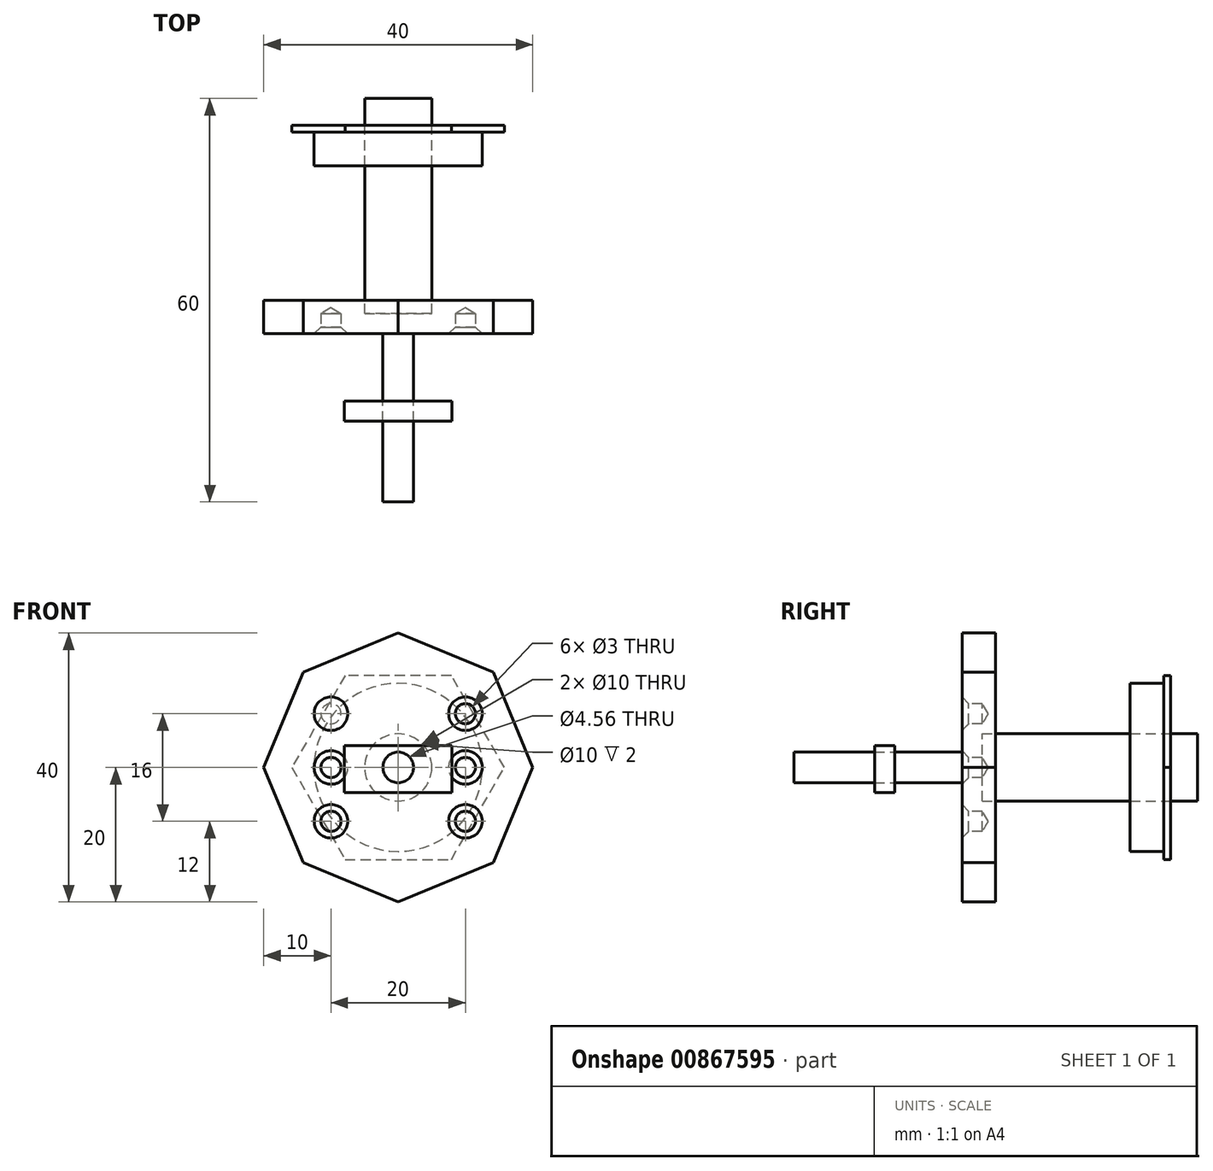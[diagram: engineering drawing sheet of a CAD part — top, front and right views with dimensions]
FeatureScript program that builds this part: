
annotation { "Feature Type Name" : "Feature", "Feature Type Description" : "" }
export const myFeature = defineFeature(function(context is Context, id is Id, definition is map)
    precondition{}
    {
        {
            var Q0;
            Q0=qCreatedBy(makeId("Front.planeOp"),FACE);
            var sketch = newSketch(context, id + "F0", { "sketchPlane" : qUnion([Q0])});
            skCircle(sketch, "E0", {"center": v(0, 0) * mm, "radius": 12.5 * mm});
            skSolve(sketch);
        }
        {
            var Q0;
            Q0 = qSketchRegion(id + "F0", true);
            extrude(context, id + "F1", {"entities" : qUnion([Q0]), "depth" : 5 * mm, "offsetDistance" : 25 * mm});
        }
        {
            var Q0;
            Q0=qCreatedBy(makeId("Front.planeOp"),FACE);
            cPlane(context, id + "F2", {"entities" : qUnion([Q0]), "cplaneType" : CPlaneType.OFFSET, "offset" : 5 * mm, "oppositeDirection" : true, "width" : 150 * mm, "height" : 150 * mm});
        }
        {
            var Q0;
            Q0=qCreatedBy(id+"F2.planeOp",FACE);
            var sketch = newSketch(context, id + "F3", { "sketchPlane" : qUnion([Q0])});
            skCircle(sketch, "E1", {"center": v(0, 0) * mm, "radius": 5 * mm});
            skSolve(sketch);
        }
        {
            var Q0;
            Q0 = qSketchRegion(id + "F3", true);
            extrude(context, id + "F4", {"entities" : qUnion([Q0]), "depth" : 32 * mm, "offsetDistance" : 25 * mm});
        }
        {
            var Q0;
            Q0=qCreatedBy(makeId("Front.planeOp"),FACE);
            cPlane(context, id + "F5", {"entities" : qUnion([Q0]), "cplaneType" : CPlaneType.OFFSET, "offset" : 25 * mm, "width" : 150 * mm, "height" : 150 * mm});
        }
        {
            var Q0;
            Q0=qCreatedBy(id+"F5.planeOp",FACE);
            var sketch = newSketch(context, id + "F6", { "sketchPlane" : qUnion([Q0])});
            skCircle(sketch, "E2.cCircle", {"center": v(0, 0) * mm, "radius": 18.48 * mm, "construction": true});
            skLineSegment(sketch, "E2.0", {"start": v(14.14, 14.14) * mm, "end": v(20, 0) * mm});
            skLineSegment(sketch, "E2.1", {"start": v(20, 0) * mm, "end": v(14.14, -14.14) * mm});
            skLineSegment(sketch, "E2.2", {"start": v(14.14, -14.14) * mm, "end": v(0, -20) * mm});
            skLineSegment(sketch, "E2.3", {"start": v(0, -20) * mm, "end": v(-14.14, -14.14) * mm});
            skLineSegment(sketch, "E2.4", {"start": v(-14.14, -14.14) * mm, "end": v(-20, 0) * mm});
            skLineSegment(sketch, "E2.5", {"start": v(-20, 0) * mm, "end": v(-14.14, 14.14) * mm});
            skLineSegment(sketch, "E2.6", {"start": v(-14.14, 14.14) * mm, "end": v(0, 20) * mm});
            skLineSegment(sketch, "E2.7", {"start": v(0, 20) * mm, "end": v(14.14, 14.14) * mm});
            skPoint(sketch, "E2.0.midPoint", {"position": v(17.07, 7.07) * mm});
            skSolve(sketch);
        }
        {
            var Q0;
            Q0 = qSketchRegion(id + "F6", true);
            extrude(context, id + "F7", {"entities" : qUnion([Q0]), "depth" : 5 * mm, "offsetDistance" : 25 * mm});
        }
        {
            var Q0;
            Q0=makeQuery(id+"F7.opExtrude","CAP_FACE",FACE,{"disambiguationData":[OSD([sQuery(id+"F6.wireOp",EDGE,"E2.0"),sQuery(id+"F6.wireOp",EDGE,"E2.1"),sQuery(id+"F6.wireOp",EDGE,"E2.2"),sQuery(id+"F6.wireOp",EDGE,"E2.3"),sQuery(id+"F6.wireOp",EDGE,"E2.4"),sQuery(id+"F6.wireOp",EDGE,"E2.5"),sQuery(id+"F6.wireOp",EDGE,"E2.6"),sQuery(id+"F6.wireOp",EDGE,"E2.7")])],"isStart":false});
            var sketch = newSketch(context, id + "F8", { "sketchPlane" : qUnion([Q0])});
            skPoint(sketch, "E3", {"position": v(-10, 0) * mm});
            skPoint(sketch, "E4", {"position": v(-10, 8) * mm});
            skPoint(sketch, "E5", {"position": v(-10, -8) * mm});
            skPoint(sketch, "E6.MirrorP", {"position": v(10, 8) * mm});
            skPoint(sketch, "E7.MirrorP", {"position": v(10, 0) * mm});
            skPoint(sketch, "E8.MirrorP", {"position": v(10, -8) * mm});
            skSolve(sketch);
        }
        {
            var Q0;
            Q0=sQuery(id+"F8.wireOp",VERTEX,"E4");
            var Q1;
            Q1=sQuery(id+"F8.wireOp",VERTEX,"E3");
            var Q2;
            Q2=sQuery(id+"F8.wireOp",VERTEX,"E5");
            var Q3;
            Q3=sQuery(id+"F8.wireOp",VERTEX,"E6.MirrorP");
            var Q4;
            Q4=sQuery(id+"F8.wireOp",VERTEX,"E7.MirrorP");
            var Q5;
            Q5=sQuery(id+"F8.wireOp",VERTEX,"E8.MirrorP");
            var Q6;
            Q6=makeQuery(id+"F7.opExtrude","SWEPT_BODY",BODY,{"disambiguationData":[OSD([sQuery(id+"F6.wireOp",EDGE,"E2.0"),sQuery(id+"F6.wireOp",EDGE,"E2.1"),sQuery(id+"F6.wireOp",EDGE,"E2.2"),sQuery(id+"F6.wireOp",EDGE,"E2.3"),sQuery(id+"F6.wireOp",EDGE,"E2.4"),sQuery(id+"F6.wireOp",EDGE,"E2.5"),sQuery(id+"F6.wireOp",EDGE,"E2.6"),sQuery(id+"F6.wireOp",EDGE,"E2.7")])]});
            hole(context, id + "F9", {"style" : HoleStyle.C_SINK, "endStyle" : HoleEndStyle.BLIND, "holeDiameter" : 3 * mm, "cSinkDiameter" : 5 * mm, "cSinkAngle" : 90 * degree, "majorDiameter" : 5 * mm, "holeDepth" : 3 * mm, "isTappedThrough" : true, "tappedDepth" : 12 * mm, "tapClearance" : 3, "startFromSketch" : true, "locations" : qUnion([Q0, Q1, Q2, Q3, Q4, Q5]), "scope" : qUnion([Q6])});
        }
        {
            var Q0;
            Q0=makeQuery(id+"F7.opExtrude","CAP_FACE",FACE,{"disambiguationData":[OSD([sQuery(id+"F6.wireOp",EDGE,"E2.0"),sQuery(id+"F6.wireOp",EDGE,"E2.1"),sQuery(id+"F6.wireOp",EDGE,"E2.2"),sQuery(id+"F6.wireOp",EDGE,"E2.3"),sQuery(id+"F6.wireOp",EDGE,"E2.4"),sQuery(id+"F6.wireOp",EDGE,"E2.5"),sQuery(id+"F6.wireOp",EDGE,"E2.6"),sQuery(id+"F6.wireOp",EDGE,"E2.7")])],"isStart":false});
            var sketch = newSketch(context, id + "F10", { "sketchPlane" : qUnion([Q0])});
            skCircle(sketch, "E9.0", {"center": v(-10, 8) * mm, "radius": 2.5 * mm});
            skSolve(sketch);
        }
        {
            var Q0;
            Q0 = qSketchRegion(id + "F10", true);
            var Q1;
            Q1=makeQuery(id+"F7.opExtrude","CAP_FACE",FACE,{"disambiguationData":[OSD([sQuery(id+"F6.wireOp",EDGE,"E2.0"),sQuery(id+"F6.wireOp",EDGE,"E2.1"),sQuery(id+"F6.wireOp",EDGE,"E2.2"),sQuery(id+"F6.wireOp",EDGE,"E2.3"),sQuery(id+"F6.wireOp",EDGE,"E2.4"),sQuery(id+"F6.wireOp",EDGE,"E2.5"),sQuery(id+"F6.wireOp",EDGE,"E2.6"),sQuery(id+"F6.wireOp",EDGE,"E2.7")])],"isStart":true});
            extrude(context, id + "F11", {"entities" : qUnion([Q0]), "endBound" : BoundingType.UP_TO_SURFACE, "oppositeDirection" : true, "depth" : 3 * mm, "endBoundEntityFace" : qUnion([Q1]), "offsetDistance" : 25 * mm});
        }
        {
            var Q0;
            Q0=makeQuery(id+"F7.opExtrude","SWEPT_BODY",BODY,{"disambiguationData":[OSD([sQuery(id+"F6.wireOp",EDGE,"E2.0"),sQuery(id+"F6.wireOp",EDGE,"E2.1"),sQuery(id+"F6.wireOp",EDGE,"E2.2"),sQuery(id+"F6.wireOp",EDGE,"E2.3"),sQuery(id+"F6.wireOp",EDGE,"E2.4"),sQuery(id+"F6.wireOp",EDGE,"E2.5"),sQuery(id+"F6.wireOp",EDGE,"E2.6"),sQuery(id+"F6.wireOp",EDGE,"E2.7")])]});
            var Q1;
            Q1=makeQuery(id+"F11.opExtrude","SWEPT_BODY",BODY,{"disambiguationData":[OSD([sQuery(id+"F10.wireOp",EDGE,"E9.0")])]});
            booleanBodies(context, id + "F12", {"operationType" : BooleanOperationType.SUBTRACTION, "tools" : qUnion([Q0]), "targets" : qUnion([Q1]), "keepTools" : true});
        }
        {
            var Q0;
            Q0=makeQuery(id+"F4.opExtrude","SWEPT_BODY",BODY,{"disambiguationData":[OSD([sQuery(id+"F3.wireOp",EDGE,"E1")])]});
            var Q1;
            Q1=makeQuery(id+"F7.opExtrude","SWEPT_BODY",BODY,{"disambiguationData":[OSD([sQuery(id+"F6.wireOp",EDGE,"E2.0"),sQuery(id+"F6.wireOp",EDGE,"E2.1"),sQuery(id+"F6.wireOp",EDGE,"E2.2"),sQuery(id+"F6.wireOp",EDGE,"E2.3"),sQuery(id+"F6.wireOp",EDGE,"E2.4"),sQuery(id+"F6.wireOp",EDGE,"E2.5"),sQuery(id+"F6.wireOp",EDGE,"E2.6"),sQuery(id+"F6.wireOp",EDGE,"E2.7")])]});
            booleanBodies(context, id + "F13", {"operationType" : BooleanOperationType.SUBTRACTION, "tools" : qUnion([Q0]), "targets" : qUnion([Q1]), "keepTools" : true});
        }
        {
            var Q0;
            Q0=makeQuery(id+"F4.opExtrude","SWEPT_BODY",BODY,{"disambiguationData":[OSD([sQuery(id+"F3.wireOp",EDGE,"E1")])]});
            var Q1;
            Q1=makeQuery(id+"F1.opExtrude","SWEPT_BODY",BODY,{"disambiguationData":[OSD([sQuery(id+"F0.wireOp",EDGE,"E0")])]});
            booleanBodies(context, id + "F14", {"operationType" : BooleanOperationType.SUBTRACTION, "tools" : qUnion([Q0]), "targets" : qUnion([Q1]), "keepTools" : true});
        }
        {
            var Q0;
            Q0=makeQuery(id+"F1.opExtrude","CAP_FACE",FACE,{"disambiguationData":[OSD([sQuery(id+"F0.wireOp",EDGE,"E0")])],"isStart":true});
            cPlane(context, id + "F15", {"entities" : qUnion([Q0]), "cplaneType" : CPlaneType.OFFSET, "offset" : 0 * mm, "width" : 150 * mm, "height" : 150 * mm});
        }
        {
            var Q0;
            Q0=qCreatedBy(id+"F15.planeOp",FACE);
            var sketch = newSketch(context, id + "F16", { "sketchPlane" : qUnion([Q0])});
            skCircle(sketch, "E10.cCircle", {"center": v(0, 0) * mm, "radius": 13.68 * mm, "construction": true});
            skLineSegment(sketch, "E10.0", {"start": v(15.8, 0) * mm, "end": v(7.9, -13.68) * mm});
            skLineSegment(sketch, "E10.1", {"start": v(7.9, -13.68) * mm, "end": v(-7.9, -13.68) * mm});
            skLineSegment(sketch, "E10.2", {"start": v(-7.9, -13.68) * mm, "end": v(-15.8, 0) * mm});
            skLineSegment(sketch, "E10.3", {"start": v(-15.8, 0) * mm, "end": v(-7.9, 13.68) * mm});
            skLineSegment(sketch, "E10.4", {"start": v(-7.9, 13.68) * mm, "end": v(7.9, 13.68) * mm});
            skLineSegment(sketch, "E10.5", {"start": v(7.9, 13.68) * mm, "end": v(15.8, 0) * mm});
            skPoint(sketch, "E10.0.midPoint", {"position": v(11.85, -6.84) * mm});
            skSolve(sketch);
        }
        {
            var Q0;
            Q0 = qSketchRegion(id + "F16", true);
            extrude(context, id + "F17", {"entities" : qUnion([Q0]), "depth" : 1 * mm, "offsetDistance" : 25 * mm});
        }
        {
            var Q0;
            Q0=makeQuery(id+"F4.opExtrude","SWEPT_BODY",BODY,{"disambiguationData":[OSD([sQuery(id+"F3.wireOp",EDGE,"E1")])]});
            var Q1;
            Q1=makeQuery(id+"F17.opExtrude","SWEPT_BODY",BODY,{"disambiguationData":[OSD([sQuery(id+"F16.wireOp",EDGE,"E10.0"),sQuery(id+"F16.wireOp",EDGE,"E10.1"),sQuery(id+"F16.wireOp",EDGE,"E10.2"),sQuery(id+"F16.wireOp",EDGE,"E10.3"),sQuery(id+"F16.wireOp",EDGE,"E10.4"),sQuery(id+"F16.wireOp",EDGE,"E10.5")])]});
            booleanBodies(context, id + "F18", {"operationType" : BooleanOperationType.SUBTRACTION, "tools" : qUnion([Q0]), "targets" : qUnion([Q1]), "keepTools" : true});
        }
        {
            var Q0;
            Q0=makeQuery(id+"F7.opExtrude","CAP_FACE",FACE,{"disambiguationData":[OSD([sQuery(id+"F6.wireOp",EDGE,"E2.0"),sQuery(id+"F6.wireOp",EDGE,"E2.1"),sQuery(id+"F6.wireOp",EDGE,"E2.2"),sQuery(id+"F6.wireOp",EDGE,"E2.3"),sQuery(id+"F6.wireOp",EDGE,"E2.4"),sQuery(id+"F6.wireOp",EDGE,"E2.5"),sQuery(id+"F6.wireOp",EDGE,"E2.6"),sQuery(id+"F6.wireOp",EDGE,"E2.7")])],"isStart":false});
            var sketch = newSketch(context, id + "F19", { "sketchPlane" : qUnion([Q0])});
            skCircle(sketch, "E11", {"center": v(0, 0) * mm, "radius": 2.28 * mm});
            skSolve(sketch);
        }
        {
            var Q0;
            Q0 = qSketchRegion(id + "F19", true);
            extrude(context, id + "F20", {"entities" : qUnion([Q0]), "operationType" : NewBodyOperationType.ADD, "depth" : 25 * mm, "offsetDistance" : 25 * mm});
        }
        {
            var Q0;
            Q0=qCreatedBy(id+"F5.planeOp",FACE);
            cPlane(context, id + "F21", {"entities" : qUnion([Q0]), "cplaneType" : CPlaneType.OFFSET, "offset" : 15 * mm, "width" : 150 * mm, "height" : 150 * mm});
        }
        {
            var Q0;
            Q0=qCreatedBy(id+"F21.planeOp",FACE);
            var sketch = newSketch(context, id + "F22", { "sketchPlane" : qUnion([Q0])});
            skLineSegment(sketch, "E12.bottom", {"start": v(7.96, 3.25) * mm, "end": v(-8.04, 3.25) * mm});
            skLineSegment(sketch, "E12.top", {"start": v(7.96, -3.75) * mm, "end": v(-8.04, -3.75) * mm});
            skLineSegment(sketch, "E12.left", {"start": v(7.96, 3.25) * mm, "end": v(7.96, -3.75) * mm});
            skLineSegment(sketch, "E12.right", {"start": v(-8.04, 3.25) * mm, "end": v(-8.04, -3.75) * mm});
            skPoint(sketch, "E12.middle", {"position": v(-0.04, -0.25) * mm});
            skSolve(sketch);
        }
        {
            var Q0;
            Q0 = qSketchRegion(id + "F22", true);
            extrude(context, id + "F23", {"entities" : qUnion([Q0]), "depth" : 3 * mm, "offsetDistance" : 25 * mm});
        }
        {
            var Q0;
            Q0=makeQuery(id+"F7.opExtrude","SWEPT_BODY",BODY,{"disambiguationData":[OSD([sQuery(id+"F6.wireOp",EDGE,"E2.0"),sQuery(id+"F6.wireOp",EDGE,"E2.1"),sQuery(id+"F6.wireOp",EDGE,"E2.2"),sQuery(id+"F6.wireOp",EDGE,"E2.3"),sQuery(id+"F6.wireOp",EDGE,"E2.4"),sQuery(id+"F6.wireOp",EDGE,"E2.5"),sQuery(id+"F6.wireOp",EDGE,"E2.6"),sQuery(id+"F6.wireOp",EDGE,"E2.7")])]});
            var Q1;
            Q1=makeQuery(id+"F23.opExtrude","SWEPT_BODY",BODY,{"disambiguationData":[OSD([sQuery(id+"F22.wireOp",EDGE,"E12.bottom"),sQuery(id+"F22.wireOp",EDGE,"E12.top"),sQuery(id+"F22.wireOp",EDGE,"E12.left"),sQuery(id+"F22.wireOp",EDGE,"E12.right")])]});
            booleanBodies(context, id + "F24", {"operationType" : BooleanOperationType.SUBTRACTION, "tools" : qUnion([Q0]), "targets" : qUnion([Q1]), "keepTools" : true});
        }
    });
